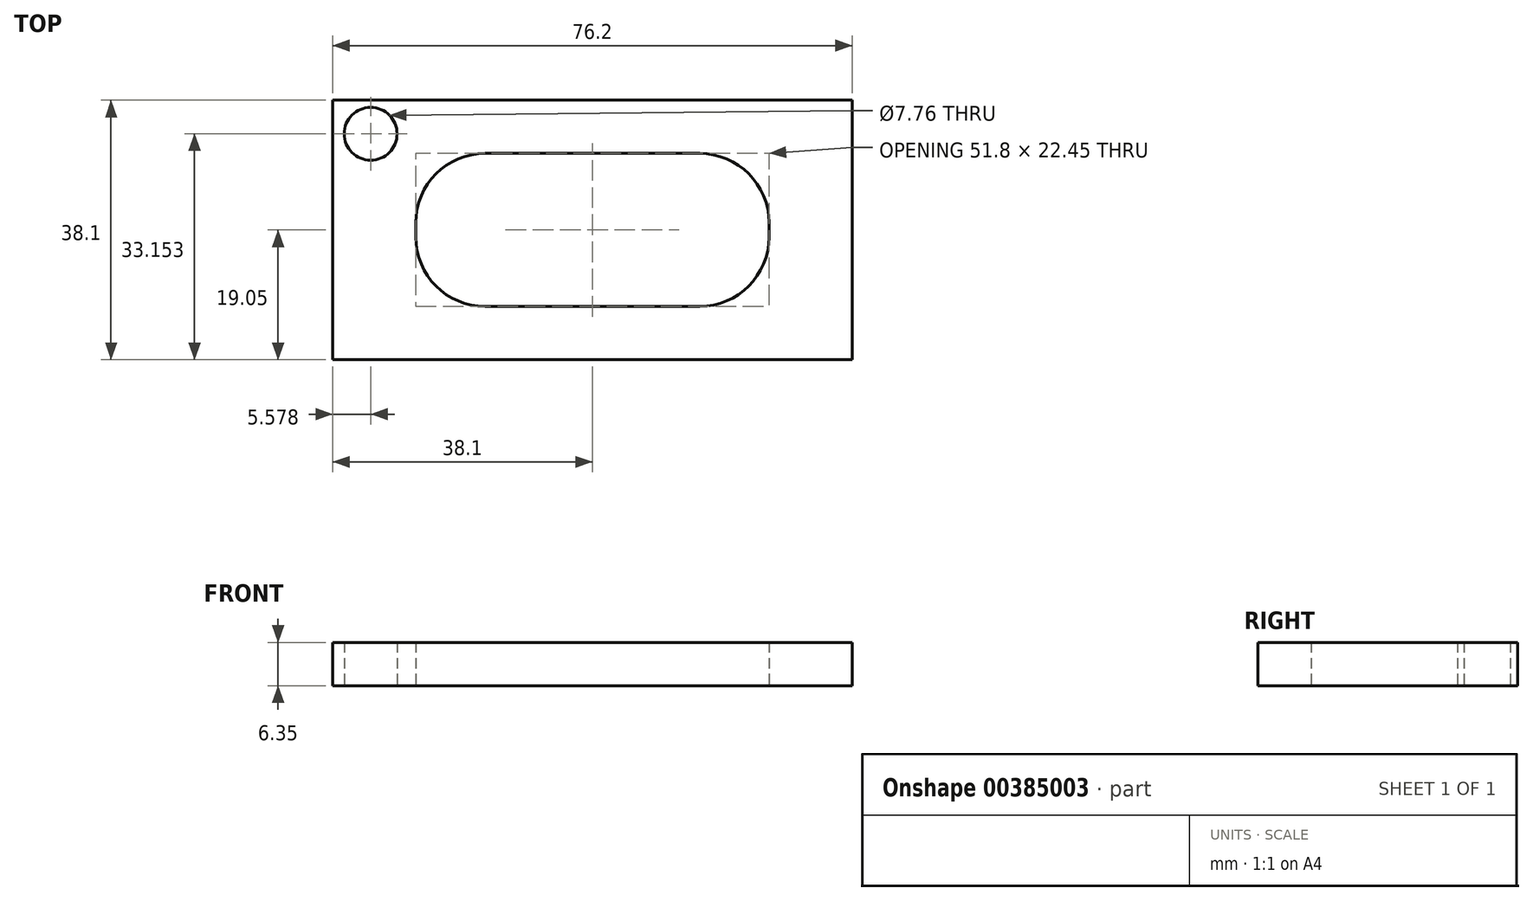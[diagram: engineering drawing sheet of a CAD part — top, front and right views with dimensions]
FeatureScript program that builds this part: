
annotation { "Feature Type Name" : "Feature", "Feature Type Description" : "" }
export const myFeature = defineFeature(function(context is Context, id is Id, definition is map)
    precondition{}
    {
        {
            var Q0;
            Q0=qCreatedBy(makeId("Top.planeOp"),FACE);
            var sketch = newSketch(context, id + "F0", { "sketchPlane" : qUnion([Q0])});
            skLineSegment(sketch, "E0.bottom", {"start": v(-38.1, -19.05) * mm, "end": v(38.1, -19.05) * mm});
            skLineSegment(sketch, "E0.top", {"start": v(-38.1, 19.05) * mm, "end": v(38.1, 19.05) * mm});
            skLineSegment(sketch, "E0.left", {"start": v(-38.1, -19.05) * mm, "end": v(-38.1, 19.05) * mm});
            skLineSegment(sketch, "E0.right", {"start": v(38.1, -19.05) * mm, "end": v(38.1, 19.05) * mm});
            skPoint(sketch, "E0.middle", {"position": v(0, 0) * mm});
            skLineSegment(sketch, "E1.bottom", {"start": v(-15.74, -11.22) * mm, "end": v(15.74, -11.22) * mm});
            skLineSegment(sketch, "E1.top", {"start": v(-15.74, 11.22) * mm, "end": v(15.74, 11.22) * mm});
            skLineSegment(sketch, "E1.left", {"start": v(-25.9, -1.06) * mm, "end": v(-25.9, 1.06) * mm});
            skLineSegment(sketch, "E1.right", {"start": v(25.9, -1.06) * mm, "end": v(25.9, 1.06) * mm});
            skPoint(sketch, "E2.visualSharp", {"position": v(-25.9, 11.22) * mm});
            skArc(sketch, "E2.filletArc", {"start": v(-15.74, 11.22) * mm, "mid": v(-22.93, 8.25) * mm, "end": v(-25.9, 1.06) * mm});
            skPoint(sketch, "E3.visualSharp", {"position": v(-25.9, -11.22) * mm});
            skArc(sketch, "E3.filletArc", {"start": v(-25.9, -1.06) * mm, "mid": v(-22.93, -8.25) * mm, "end": v(-15.74, -11.22) * mm});
            skPoint(sketch, "E4.visualSharp", {"position": v(25.9, 11.22) * mm});
            skArc(sketch, "E4.filletArc", {"start": v(25.9, 1.06) * mm, "mid": v(22.93, 8.25) * mm, "end": v(15.74, 11.22) * mm});
            skPoint(sketch, "E5.visualSharp", {"position": v(25.9, -11.22) * mm});
            skArc(sketch, "E5.filletArc", {"start": v(15.74, -11.22) * mm, "mid": v(22.93, -8.25) * mm, "end": v(25.9, -1.06) * mm});
            skCircle(sketch, "E6", {"center": v(-32.52, 14.1) * mm, "radius": 3.88 * mm});
            skSolve(sketch);
        }
        {
            var Q0;
            Q0 = qSketchRegion(id + "F0", true);
            extrude(context, id + "F1", {"entities" : qUnion([Q0]), "depth" : 6.35 * mm});
        }
    });
